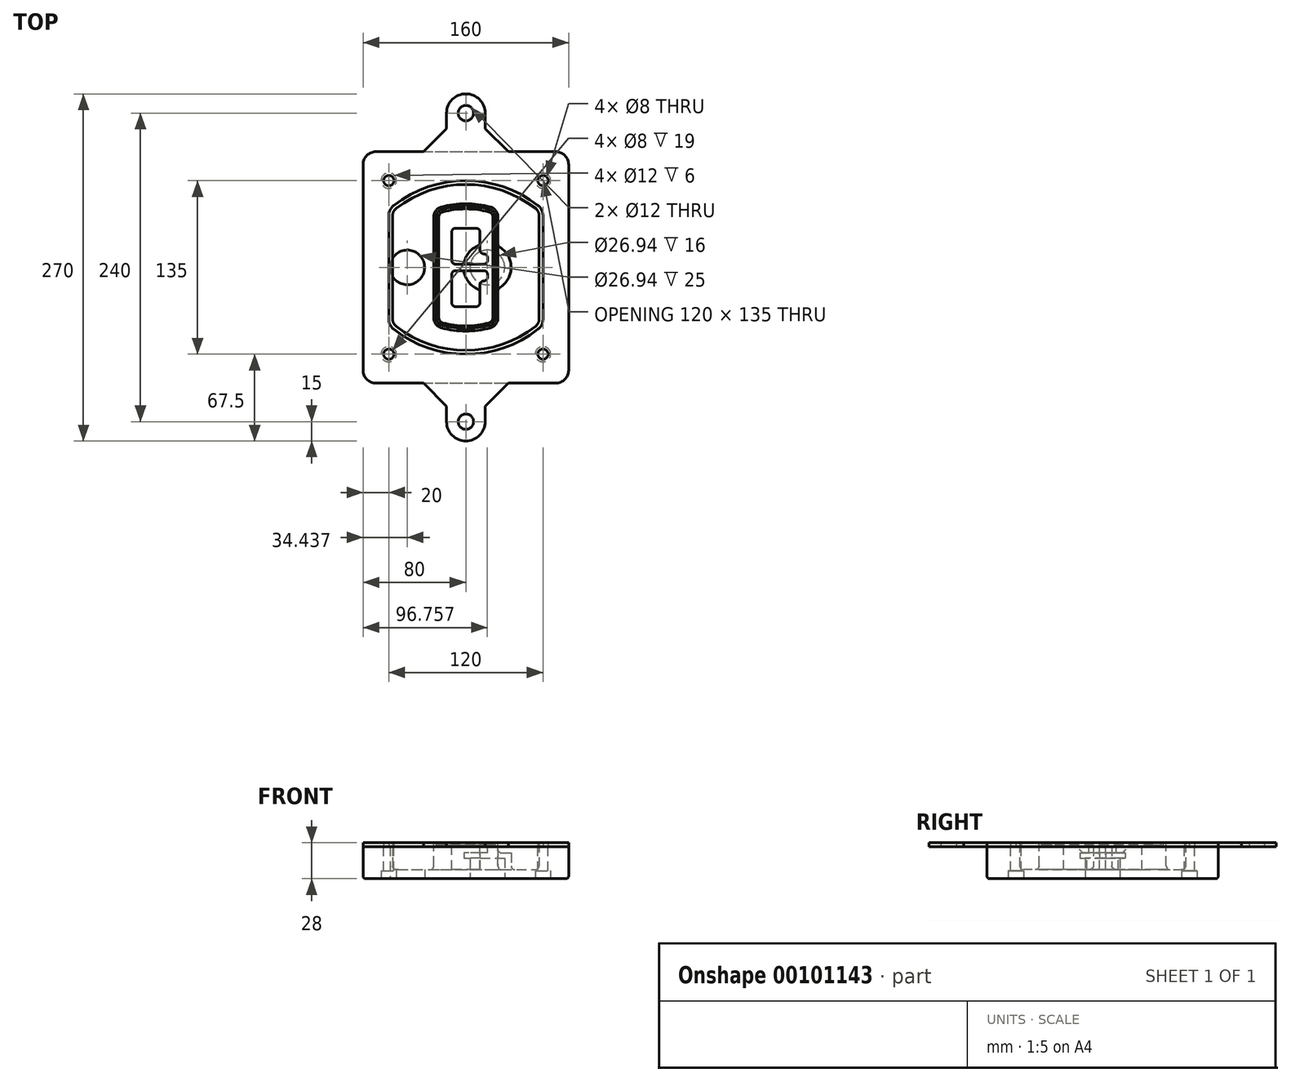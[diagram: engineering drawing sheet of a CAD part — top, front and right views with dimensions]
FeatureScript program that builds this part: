
annotation { "Feature Type Name" : "Feature", "Feature Type Description" : "" }
export const myFeature = defineFeature(function(context is Context, id is Id, definition is map)
    precondition{}
    {
        {
            var Q0;
            Q0=qCreatedBy(makeId("Top.planeOp"),FACE);
            var sketch = newSketch(context, id + "F0", { "sketchPlane" : qUnion([Q0])});
            skPoint(sketch, "E0.rect.middle", {"position": v(0, 0) * mm});
            skLineSegment(sketch, "E1.bottom", {"start": v(-70, -90) * mm, "end": v(70, -90) * mm});
            skLineSegment(sketch, "E1.top", {"start": v(-70, 90) * mm, "end": v(70, 90) * mm});
            skLineSegment(sketch, "E1.left", {"start": v(-80, -80) * mm, "end": v(-80, 80) * mm});
            skLineSegment(sketch, "E1.right", {"start": v(80, -80) * mm, "end": v(80, 80) * mm});
            skLineSegment(sketch, "E2", {"start": v(-80, 90) * mm, "end": v(80, -90) * mm, "construction": true});
            skLineSegment(sketch, "E3", {"start": v(80, 90) * mm, "end": v(-80, -90) * mm, "construction": true});
            skCircle(sketch, "E4", {"center": v(-60, 67.5) * mm, "radius": 4 * mm});
            skCircle(sketch, "E5", {"center": v(60, 67.5) * mm, "radius": 4 * mm});
            skCircle(sketch, "E6", {"center": v(60, -67.5) * mm, "radius": 4 * mm});
            skCircle(sketch, "E7", {"center": v(-60, -67.5) * mm, "radius": 4 * mm});
            skLineSegment(sketch, "E8", {"start": v(-60, 67.5) * mm, "end": v(60, 67.5) * mm, "construction": true});
            skLineSegment(sketch, "E9", {"start": v(60, 67.5) * mm, "end": v(60, -67.5) * mm, "construction": true});
            skLineSegment(sketch, "E10", {"start": v(60, -67.5) * mm, "end": v(-60, -67.5) * mm, "construction": true});
            skLineSegment(sketch, "E11", {"start": v(-60, -67.5) * mm, "end": v(-60, 67.5) * mm, "construction": true});
            skLineSegment(sketch, "E12", {"start": v(-60, 40.3) * mm, "end": v(-60, -40.3) * mm});
            skLineSegment(sketch, "E13", {"start": v(60, 40.3) * mm, "end": v(60, -40.3) * mm});
            skArc(sketch, "E14", {"start": v(56.15, 48.18) * mm, "mid": v(0, 67.5) * mm, "end": v(-56.15, 48.18) * mm});
            skArc(sketch, "E15", {"start": v(-56.15, -48.18) * mm, "mid": v(0, -67.5) * mm, "end": v(56.15, -48.18) * mm});
            skLineSegment(sketch, "E16", {"start": v(-60, 0) * mm, "end": v(60, 0) * mm, "construction": true});
            skPoint(sketch, "E17.visualSharp", {"position": v(-60, -45) * mm});
            skArc(sketch, "E17.filletArc", {"start": v(-60, -40.3) * mm, "mid": v(-58.99, -44.68) * mm, "end": v(-56.15, -48.18) * mm});
            skPoint(sketch, "E18.visualSharp", {"position": v(-60, 45) * mm});
            skArc(sketch, "E18.filletArc", {"start": v(-56.15, 48.18) * mm, "mid": v(-58.99, 44.68) * mm, "end": v(-60, 40.3) * mm});
            skPoint(sketch, "E19.visualSharp", {"position": v(60, 45) * mm});
            skArc(sketch, "E19.filletArc", {"start": v(60, 40.3) * mm, "mid": v(58.99, 44.68) * mm, "end": v(56.15, 48.18) * mm});
            skPoint(sketch, "E20.visualSharp", {"position": v(60, -45) * mm});
            skArc(sketch, "E20.filletArc", {"start": v(56.15, -48.18) * mm, "mid": v(58.99, -44.68) * mm, "end": v(60, -40.3) * mm});
            skPoint(sketch, "E21.visualSharp", {"position": v(-80, 90) * mm});
            skArc(sketch, "E21.filletArc", {"start": v(-70, 90) * mm, "mid": v(-77.07, 87.07) * mm, "end": v(-80, 80) * mm});
            skPoint(sketch, "E22.visualSharp", {"position": v(80, 90) * mm});
            skArc(sketch, "E22.filletArc", {"start": v(80, 80) * mm, "mid": v(77.07, 87.07) * mm, "end": v(70, 90) * mm});
            skPoint(sketch, "E23.visualSharp", {"position": v(80, -90) * mm});
            skArc(sketch, "E23.filletArc", {"start": v(70, -90) * mm, "mid": v(77.07, -87.07) * mm, "end": v(80, -80) * mm});
            skPoint(sketch, "E24.visualSharp", {"position": v(-80, -90) * mm});
            skArc(sketch, "E24.filletArc", {"start": v(-80, -80) * mm, "mid": v(-77.07, -87.07) * mm, "end": v(-70, -90) * mm});
            skArc(sketch, "E25.0", {"start": v(57, 40.3) * mm, "mid": v(56.3, 43.36) * mm, "end": v(54.3, 45.81) * mm});
            skLineSegment(sketch, "E25.1", {"start": v(57, 40.3) * mm, "end": v(57, -40.3) * mm});
            skArc(sketch, "E25.2", {"start": v(54.3, -45.81) * mm, "mid": v(56.3, -43.36) * mm, "end": v(57, -40.3) * mm});
            skArc(sketch, "E25.3", {"start": v(-54.3, -45.81) * mm, "mid": v(0, -64.5) * mm, "end": v(54.3, -45.81) * mm});
            skArc(sketch, "E25.4", {"start": v(-57, -40.3) * mm, "mid": v(-56.3, -43.36) * mm, "end": v(-54.3, -45.81) * mm});
            skArc(sketch, "E25.5", {"start": v(54.3, 45.81) * mm, "mid": v(0, 64.5) * mm, "end": v(-54.3, 45.81) * mm});
            skLineSegment(sketch, "E25.6", {"start": v(-57, 40.3) * mm, "end": v(-57, -40.3) * mm});
            skArc(sketch, "E25.7", {"start": v(-54.3, 45.81) * mm, "mid": v(-56.3, 43.36) * mm, "end": v(-57, 40.3) * mm});
            skArc(sketch, "E26.0", {"start": v(-58.62, 51.33) * mm, "mid": v(-62.58, 46.43) * mm, "end": v(-64, 40.3) * mm});
            skArc(sketch, "E26.1", {"start": v(58.62, 51.33) * mm, "mid": v(0, 71.5) * mm, "end": v(-58.62, 51.33) * mm});
            skArc(sketch, "E26.2", {"start": v(64, 40.3) * mm, "mid": v(62.58, 46.43) * mm, "end": v(58.62, 51.33) * mm});
            skLineSegment(sketch, "E26.3", {"start": v(64, 40.3) * mm, "end": v(64, -40.3) * mm});
            skArc(sketch, "E26.4", {"start": v(58.62, -51.33) * mm, "mid": v(62.58, -46.43) * mm, "end": v(64, -40.3) * mm});
            skLineSegment(sketch, "E26.5", {"start": v(-64, 40.3) * mm, "end": v(-64, -40.3) * mm});
            skArc(sketch, "E26.6", {"start": v(-58.62, -51.33) * mm, "mid": v(0, -71.5) * mm, "end": v(58.62, -51.33) * mm});
            skArc(sketch, "E26.7", {"start": v(-64, -40.3) * mm, "mid": v(-62.58, -46.43) * mm, "end": v(-58.62, -51.33) * mm});
            skSolve(sketch);
        }
        {
            var Q0;
            Q0=makeQuery(id+"F0.imprint","IMPRINT",FACE,{"disambiguationData":[TD([[makeQuery(id+"F0.imprint","IMPRINT",EDGE,{"derivedFrom":sQuery(id+"F0.wireOp",EDGE,"E1.bottom")}),1.0]])]});
            var Q1;
            Q1=makeQuery(id+"F0.imprint","IMPRINT",FACE,{"disambiguationData":[TD([[makeQuery(id+"F0.imprint","IMPRINT",EDGE,{"derivedFrom":sQuery(id+"F0.wireOp",EDGE,"E12")}),1.0]])]});
            var Q2;
            Q2=makeQuery(id+"F0.imprint","IMPRINT",FACE,{"disambiguationData":[TD([[makeQuery(id+"F0.imprint","IMPRINT",EDGE,{"derivedFrom":sQuery(id+"F0.wireOp",EDGE,"E25.0")}),1.0]])]});
            var Q3;
            Q3=makeQuery(id+"F0.imprint","IMPRINT",FACE,{"disambiguationData":[TD([[makeQuery(id+"F0.imprint","IMPRINT",EDGE,{"derivedFrom":sQuery(id+"F0.wireOp",EDGE,"E12")}),-1.0]])]});
            extrude(context, id + "F1", {"entities" : qUnion([Q0, Q1, Q2, Q3]), "oppositeDirection" : true, "depth" : 25 * mm});
        }
        {
            var Q0;
            Q0=makeQuery(id+"F0.imprint","IMPRINT",FACE,{"disambiguationData":[TD([[makeQuery(id+"F0.imprint","IMPRINT",EDGE,{"derivedFrom":sQuery(id+"F0.wireOp",EDGE,"E12")}),1.0]])]});
            extrude(context, id + "F2", {"entities" : qUnion([Q0]), "operationType" : NewBodyOperationType.ADD, "depth" : 3 * mm});
        }
        {
            var Q0;
            Q0=makeQuery(id+"F0.imprint","IMPRINT",FACE,{"disambiguationData":[TD([[makeQuery(id+"F0.imprint","IMPRINT",EDGE,{"derivedFrom":sQuery(id+"F0.wireOp",EDGE,"E25.0")}),1.0]])]});
            extrude(context, id + "F3", {"entities" : qUnion([Q0]), "operationType" : NewBodyOperationType.REMOVE, "oppositeDirection" : true, "depth" : 18 * mm});
        }
        {
            var Q0;
            Q0=makeQuery(id+"F2.opExtrude","CAP_FACE",FACE,{"disambiguationData":[OSD([sQuery(id+"F0.wireOp",EDGE,"E12"),sQuery(id+"F0.wireOp",EDGE,"E13"),sQuery(id+"F0.wireOp",EDGE,"E14"),sQuery(id+"F0.wireOp",EDGE,"E15"),sQuery(id+"F0.wireOp",EDGE,"E17.filletArc"),sQuery(id+"F0.wireOp",EDGE,"E18.filletArc"),sQuery(id+"F0.wireOp",EDGE,"E19.filletArc"),sQuery(id+"F0.wireOp",EDGE,"E20.filletArc"),sQuery(id+"F0.wireOp",EDGE,"E25.0"),sQuery(id+"F0.wireOp",EDGE,"E25.1"),sQuery(id+"F0.wireOp",EDGE,"E25.2"),sQuery(id+"F0.wireOp",EDGE,"E25.3"),sQuery(id+"F0.wireOp",EDGE,"E25.4"),sQuery(id+"F0.wireOp",EDGE,"E25.5"),sQuery(id+"F0.wireOp",EDGE,"E25.6"),sQuery(id+"F0.wireOp",EDGE,"E25.7")])],"isStart":false});
            var sketch = newSketch(context, id + "F4", { "sketchPlane" : qUnion([Q0])});
            skArc(sketch, "E27.0", {"start": v(-19.08, -46.97) * mm, "mid": v(0, -49.5) * mm, "end": v(19.08, -46.97) * mm});
            skArc(sketch, "E28.0", {"start": v(19.08, 46.97) * mm, "mid": v(0, 49.5) * mm, "end": v(-19.08, 46.97) * mm});
            skLineSegment(sketch, "E29", {"start": v(-25, 39.25) * mm, "end": v(-25, -39.25) * mm});
            skLineSegment(sketch, "E30", {"start": v(25, 39.25) * mm, "end": v(25, -39.25) * mm});
            skLineSegment(sketch, "E31", {"start": v(-25, 45.1) * mm, "end": v(25, 45.1) * mm, "construction": true});
            skLineSegment(sketch, "E32", {"start": v(-25, -45.1) * mm, "end": v(25, -45.1) * mm, "construction": true});
            skPoint(sketch, "E33.visualSharp", {"position": v(-25, 45.1) * mm});
            skArc(sketch, "E33.filletArc", {"start": v(-19.08, 46.97) * mm, "mid": v(-23.35, 44.11) * mm, "end": v(-25, 39.25) * mm});
            skPoint(sketch, "E34.visualSharp", {"position": v(25, 45.1) * mm});
            skArc(sketch, "E34.filletArc", {"start": v(25, 39.25) * mm, "mid": v(23.35, 44.11) * mm, "end": v(19.08, 46.97) * mm});
            skPoint(sketch, "E35.visualSharp", {"position": v(25, -45.1) * mm});
            skArc(sketch, "E35.filletArc", {"start": v(19.08, -46.97) * mm, "mid": v(23.35, -44.11) * mm, "end": v(25, -39.25) * mm});
            skPoint(sketch, "E36.visualSharp", {"position": v(-25, -45.1) * mm});
            skArc(sketch, "E36.filletArc", {"start": v(-25, -39.25) * mm, "mid": v(-23.35, -44.11) * mm, "end": v(-19.08, -46.97) * mm});
            skArc(sketch, "E37.0", {"start": v(54.3, 45.81) * mm, "mid": v(0, 64.5) * mm, "end": v(-54.3, 45.81) * mm});
            skArc(sketch, "E37.1", {"start": v(-54.3, 45.81) * mm, "mid": v(-56.3, 43.36) * mm, "end": v(-57, 40.3) * mm});
            skLineSegment(sketch, "E37.2", {"start": v(-57, 40.3) * mm, "end": v(-57, -40.3) * mm});
            skArc(sketch, "E37.3", {"start": v(-57, -40.3) * mm, "mid": v(-56.3, -43.36) * mm, "end": v(-54.3, -45.81) * mm});
            skArc(sketch, "E37.4", {"start": v(-54.3, -45.81) * mm, "mid": v(0, -64.5) * mm, "end": v(54.3, -45.81) * mm});
            skArc(sketch, "E37.5", {"start": v(54.3, -45.81) * mm, "mid": v(56.3, -43.36) * mm, "end": v(57, -40.3) * mm});
            skLineSegment(sketch, "E37.6", {"start": v(57, 40.3) * mm, "end": v(57, -40.3) * mm});
            skArc(sketch, "E37.7", {"start": v(57, 40.3) * mm, "mid": v(56.3, 43.36) * mm, "end": v(54.3, 45.81) * mm});
            skLineSegment(sketch, "E38.0", {"start": v(23, 39.25) * mm, "end": v(23, -39.25) * mm});
            skArc(sketch, "E38.1", {"start": v(18.56, -45.04) * mm, "mid": v(21.76, -42.9) * mm, "end": v(23, -39.25) * mm});
            skArc(sketch, "E38.2", {"start": v(-18.56, -45.04) * mm, "mid": v(0, -47.5) * mm, "end": v(18.56, -45.04) * mm});
            skArc(sketch, "E38.3", {"start": v(-23, -39.25) * mm, "mid": v(-21.76, -42.9) * mm, "end": v(-18.56, -45.04) * mm});
            skLineSegment(sketch, "E38.4", {"start": v(-23, 39.25) * mm, "end": v(-23, -39.25) * mm});
            skArc(sketch, "E38.5", {"start": v(23, 39.25) * mm, "mid": v(21.76, 42.9) * mm, "end": v(18.56, 45.04) * mm});
            skArc(sketch, "E38.6", {"start": v(-18.56, 45.04) * mm, "mid": v(-21.76, 42.9) * mm, "end": v(-23, 39.25) * mm});
            skArc(sketch, "E38.7", {"start": v(18.56, 45.04) * mm, "mid": v(0, 47.5) * mm, "end": v(-18.56, 45.04) * mm});
            skArc(sketch, "E39.0", {"start": v(21, 39.25) * mm, "mid": v(20.18, 41.68) * mm, "end": v(18.04, 43.1) * mm});
            skLineSegment(sketch, "E39.1", {"start": v(21, 39.25) * mm, "end": v(21, -39.25) * mm});
            skArc(sketch, "E39.2", {"start": v(18.04, -43.1) * mm, "mid": v(20.18, -41.68) * mm, "end": v(21, -39.25) * mm});
            skArc(sketch, "E39.3", {"start": v(-18.04, -43.1) * mm, "mid": v(0, -45.5) * mm, "end": v(18.04, -43.1) * mm});
            skArc(sketch, "E39.4", {"start": v(-21, -39.25) * mm, "mid": v(-20.18, -41.68) * mm, "end": v(-18.04, -43.1) * mm});
            skArc(sketch, "E39.5", {"start": v(18.04, 43.1) * mm, "mid": v(0, 45.5) * mm, "end": v(-18.04, 43.1) * mm});
            skLineSegment(sketch, "E39.6", {"start": v(-21, 39.25) * mm, "end": v(-21, -39.25) * mm});
            skArc(sketch, "E39.7", {"start": v(-18.04, 43.1) * mm, "mid": v(-20.18, 41.68) * mm, "end": v(-21, 39.25) * mm});
            skLineSegment(sketch, "E40", {"start": v(-25, 0) * mm, "end": v(25, 0) * mm, "construction": true});
            skLineSegment(sketch, "E41", {"start": v(-11, 5.5) * mm, "end": v(-11, 27.5) * mm});
            skLineSegment(sketch, "E42", {"start": v(-8, 30.5) * mm, "end": v(8, 30.5) * mm});
            skLineSegment(sketch, "E43", {"start": v(11, 27.5) * mm, "end": v(11, 13.5) * mm});
            skLineSegment(sketch, "E44", {"start": v(14, 10.5) * mm, "end": v(14, 10.5) * mm});
            skLineSegment(sketch, "E45", {"start": v(17, 7.5) * mm, "end": v(17, 5.5) * mm});
            skLineSegment(sketch, "E46", {"start": v(14, 2.5) * mm, "end": v(-8, 2.5) * mm});
            skPoint(sketch, "E47.visualSharp", {"position": v(-11, 30.5) * mm});
            skArc(sketch, "E47.filletArc", {"start": v(-8, 30.5) * mm, "mid": v(-10.12, 29.62) * mm, "end": v(-11, 27.5) * mm});
            skPoint(sketch, "E48.visualSharp", {"position": v(11, 30.5) * mm});
            skArc(sketch, "E48.filletArc", {"start": v(11, 27.5) * mm, "mid": v(10.12, 29.62) * mm, "end": v(8, 30.5) * mm});
            skPoint(sketch, "E49.visualSharp", {"position": v(11, 10.5) * mm});
            skArc(sketch, "E49.filletArc", {"start": v(11, 13.5) * mm, "mid": v(11.88, 11.38) * mm, "end": v(14, 10.5) * mm});
            skPoint(sketch, "E50.visualSharp", {"position": v(17, 10.5) * mm});
            skArc(sketch, "E50.filletArc", {"start": v(17, 7.5) * mm, "mid": v(16.12, 9.62) * mm, "end": v(14, 10.5) * mm});
            skPoint(sketch, "E51.visualSharp", {"position": v(17, 2.5) * mm});
            skArc(sketch, "E51.filletArc", {"start": v(14, 2.5) * mm, "mid": v(16.12, 3.38) * mm, "end": v(17, 5.5) * mm});
            skPoint(sketch, "E52.visualSharp", {"position": v(-11, 2.5) * mm});
            skArc(sketch, "E52.filletArc", {"start": v(-11, 5.5) * mm, "mid": v(-10.12, 3.38) * mm, "end": v(-8, 2.5) * mm});
            skLineSegment(sketch, "E53.0.MirrorCS", {"start": v(14, -2.5) * mm, "end": v(-8, -2.5) * mm});
            skArc(sketch, "E54.0.MirrorCS", {"start": v(-11, -5.5) * mm, "mid": v(-10.12, -3.38) * mm, "end": v(-8, -2.5) * mm});
            skLineSegment(sketch, "E55.0.MirrorCS", {"start": v(-11, -5.5) * mm, "end": v(-11, -27.5) * mm});
            skArc(sketch, "E56.0.MirrorCS", {"start": v(-8, -30.5) * mm, "mid": v(-10.12, -29.62) * mm, "end": v(-11, -27.5) * mm});
            skLineSegment(sketch, "E57.0.MirrorCS", {"start": v(-8, -30.5) * mm, "end": v(8, -30.5) * mm});
            skArc(sketch, "E58.0.MirrorCS", {"start": v(11, -27.5) * mm, "mid": v(10.12, -29.62) * mm, "end": v(8, -30.5) * mm});
            skLineSegment(sketch, "E59.0.MirrorCS", {"start": v(11, -27.5) * mm, "end": v(11, -13.5) * mm});
            skArc(sketch, "E60.0.MirrorCS", {"start": v(11, -13.5) * mm, "mid": v(11.88, -11.38) * mm, "end": v(14, -10.5) * mm});
            skArc(sketch, "E61.0.MirrorCS", {"start": v(17, -7.5) * mm, "mid": v(16.12, -9.62) * mm, "end": v(14, -10.5) * mm});
            skLineSegment(sketch, "E62.0.MirrorCS", {"start": v(17, -7.5) * mm, "end": v(17, -5.5) * mm});
            skArc(sketch, "E63.0.MirrorCS", {"start": v(14, -2.5) * mm, "mid": v(16.12, -3.38) * mm, "end": v(17, -5.5) * mm});
            skSolve(sketch);
        }
        {
            var Q0;
            Q0=makeQuery(id+"F4.imprint","IMPRINT",FACE,{"disambiguationData":[TD([[makeQuery(id+"F4.imprint","IMPRINT",EDGE,{"derivedFrom":sQuery(id+"F4.wireOp",EDGE,"E27.0")}),1.0]])]});
            var Q1;
            Q1=makeQuery(id+"F4.imprint","IMPRINT",FACE,{"disambiguationData":[TD([[makeQuery(id+"F4.imprint","IMPRINT",EDGE,{"derivedFrom":sQuery(id+"F4.wireOp",EDGE,"E38.0")}),-1.0]])]});
            var Q2;
            Q2=makeQuery(id+"F4.imprint","IMPRINT",FACE,{"disambiguationData":[TD([[makeQuery(id+"F4.imprint","IMPRINT",EDGE,{"derivedFrom":sQuery(id+"F4.wireOp",EDGE,"E39.0")}),1.0]])]});
            extrude(context, id + "F5", {"entities" : qUnion([Q0, Q1, Q2]), "operationType" : NewBodyOperationType.ADD, "endBound" : BoundingType.UP_TO_NEXT, "oppositeDirection" : true, "depth" : 25 * mm});
        }
        {
            var Q0;
            Q0=makeQuery(id+"F4.imprint","IMPRINT",FACE,{"disambiguationData":[TD([[makeQuery(id+"F4.imprint","IMPRINT",EDGE,{"derivedFrom":sQuery(id+"F4.wireOp",EDGE,"E38.0")}),-1.0]])]});
            extrude(context, id + "F6", {"entities" : qUnion([Q0]), "operationType" : NewBodyOperationType.REMOVE, "oppositeDirection" : true, "depth" : 2 * mm});
        }
        {
            var Q0;
            Q0=makeQuery(id+"F1.opExtrude","CAP_FACE",FACE,{"disambiguationData":[OSD([sQuery(id+"F0.wireOp",EDGE,"E1.bottom"),sQuery(id+"F0.wireOp",EDGE,"E1.top"),sQuery(id+"F0.wireOp",EDGE,"E1.left"),sQuery(id+"F0.wireOp",EDGE,"E1.right"),sQuery(id+"F0.wireOp",EDGE,"E4"),sQuery(id+"F0.wireOp",EDGE,"E5"),sQuery(id+"F0.wireOp",EDGE,"E6"),sQuery(id+"F0.wireOp",EDGE,"E7"),sQuery(id+"F0.wireOp",EDGE,"E21.filletArc"),sQuery(id+"F0.wireOp",EDGE,"E22.filletArc"),sQuery(id+"F0.wireOp",EDGE,"E23.filletArc"),sQuery(id+"F0.wireOp",EDGE,"E24.filletArc")])],"isStart":false});
            var sketch = newSketch(context, id + "F7", { "sketchPlane" : qUnion([Q0])});
            skCircle(sketch, "E64", {"center": v(16.76, 0) * mm, "radius": 13.47 * mm});
            skCircle(sketch, "E65", {"center": v(-45.56, 0) * mm, "radius": 13.47 * mm});
            skLineSegment(sketch, "E66", {"start": v(80, 0) * mm, "end": v(-80, 0) * mm});
            skCircle(sketch, "E67", {"center": v(16.76, 0) * mm, "radius": 18.47 * mm});
            skCircle(sketch, "E68", {"center": v(60, -67.5) * mm, "radius": 6 * mm});
            skCircle(sketch, "E69", {"center": v(-60, -67.5) * mm, "radius": 6 * mm});
            skCircle(sketch, "E70", {"center": v(-60, 67.5) * mm, "radius": 6 * mm});
            skCircle(sketch, "E71", {"center": v(60, 67.5) * mm, "radius": 6 * mm});
            skSolve(sketch);
        }
        {
            var Q0;
            {var subQ1=sQuery(id+"F7.wireOp",EDGE,"E66");var subQ4=sQuery(id+"F7.wireOp",EDGE,"E64");var subQ6=makeQuery(id+"F7.imprint","INTERSECT",VERTEX,{"disambiguationData":[OD(0.0)],"derivedFrom":[subQ4,subQ1]});Q0=makeQuery(id+"F7.imprint","IMPRINT",FACE,{"disambiguationData":[TD([[makeQuery(id+"F7.imprint","IMPRINT",EDGE,{"disambiguationData":[TD([[subQ6,-1.0]])],"derivedFrom":subQ4}),-1.0]])]});}
            var Q1;
            {var subQ0=sQuery(id+"F7.wireOp",EDGE,"E66");var subQ1=sQuery(id+"F7.wireOp",EDGE,"E64");var subQ3=makeQuery(id+"F7.imprint","INTERSECT",VERTEX,{"disambiguationData":[OD(0.0)],"derivedFrom":[subQ1,subQ0]});Q1=makeQuery(id+"F7.imprint","IMPRINT",FACE,{"disambiguationData":[TD([[makeQuery(id+"F7.imprint","IMPRINT",EDGE,{"disambiguationData":[TD([[subQ3,-1.0]])],"derivedFrom":subQ1}),1.0]])]});}
            var Q2;
            {var subQ0=sQuery(id+"F7.wireOp",EDGE,"E66");var subQ1=sQuery(id+"F7.wireOp",EDGE,"E64");var subQ3=makeQuery(id+"F7.imprint","INTERSECT",VERTEX,{"disambiguationData":[OD(0.0)],"derivedFrom":[subQ1,subQ0]});Q2=makeQuery(id+"F7.imprint","IMPRINT",FACE,{"disambiguationData":[TD([[makeQuery(id+"F7.imprint","IMPRINT",EDGE,{"disambiguationData":[TD([[subQ3,1.0]])],"derivedFrom":subQ1}),1.0]])]});}
            var Q3;
            {var subQ1=sQuery(id+"F7.wireOp",EDGE,"E66");var subQ4=sQuery(id+"F7.wireOp",EDGE,"E64");var subQ6=makeQuery(id+"F7.imprint","INTERSECT",VERTEX,{"disambiguationData":[OD(0.0)],"derivedFrom":[subQ4,subQ1]});Q3=makeQuery(id+"F7.imprint","IMPRINT",FACE,{"disambiguationData":[TD([[makeQuery(id+"F7.imprint","IMPRINT",EDGE,{"disambiguationData":[TD([[subQ6,1.0]])],"derivedFrom":subQ4}),-1.0]])]});}
            extrude(context, id + "F8", {"entities" : qUnion([Q0, Q1, Q2, Q3]), "operationType" : NewBodyOperationType.ADD, "oppositeDirection" : true, "depth" : 20 * mm});
        }
        {
            var Q0;
            {var subQ0=sQuery(id+"F7.wireOp",EDGE,"E66");var subQ1=sQuery(id+"F7.wireOp",EDGE,"E64");var subQ3=makeQuery(id+"F7.imprint","INTERSECT",VERTEX,{"disambiguationData":[OD(0.0)],"derivedFrom":[subQ1,subQ0]});Q0=makeQuery(id+"F7.imprint","IMPRINT",FACE,{"disambiguationData":[TD([[makeQuery(id+"F7.imprint","IMPRINT",EDGE,{"disambiguationData":[TD([[subQ3,-1.0]])],"derivedFrom":subQ1}),1.0]])]});}
            var Q1;
            {var subQ0=sQuery(id+"F7.wireOp",EDGE,"E66");var subQ1=sQuery(id+"F7.wireOp",EDGE,"E64");var subQ3=makeQuery(id+"F7.imprint","INTERSECT",VERTEX,{"disambiguationData":[OD(0.0)],"derivedFrom":[subQ1,subQ0]});Q1=makeQuery(id+"F7.imprint","IMPRINT",FACE,{"disambiguationData":[TD([[makeQuery(id+"F7.imprint","IMPRINT",EDGE,{"disambiguationData":[TD([[subQ3,1.0]])],"derivedFrom":subQ1}),1.0]])]});}
            extrude(context, id + "F9", {"entities" : qUnion([Q0, Q1]), "operationType" : NewBodyOperationType.REMOVE, "oppositeDirection" : true, "depth" : 16 * mm});
        }
        {
            var Q0;
            {var subQ0=sQuery(id+"F7.wireOp",EDGE,"E66");var subQ1=sQuery(id+"F7.wireOp",EDGE,"E65");var subQ3=makeQuery(id+"F7.imprint","INTERSECT",VERTEX,{"disambiguationData":[OD(0.0)],"derivedFrom":[subQ1,subQ0]});Q0=makeQuery(id+"F7.imprint","IMPRINT",FACE,{"disambiguationData":[TD([[makeQuery(id+"F7.imprint","IMPRINT",EDGE,{"disambiguationData":[TD([[subQ3,-1.0]])],"derivedFrom":subQ1}),1.0]])]});}
            var Q1;
            {var subQ0=sQuery(id+"F7.wireOp",EDGE,"E66");var subQ1=sQuery(id+"F7.wireOp",EDGE,"E65");var subQ3=makeQuery(id+"F7.imprint","INTERSECT",VERTEX,{"disambiguationData":[OD(0.0)],"derivedFrom":[subQ1,subQ0]});Q1=makeQuery(id+"F7.imprint","IMPRINT",FACE,{"disambiguationData":[TD([[makeQuery(id+"F7.imprint","IMPRINT",EDGE,{"disambiguationData":[TD([[subQ3,1.0]])],"derivedFrom":subQ1}),1.0]])]});}
            extrude(context, id + "F10", {"entities" : qUnion([Q0, Q1]), "operationType" : NewBodyOperationType.REMOVE, "oppositeDirection" : true, "depth" : 25 * mm});
        }
        {
            var Q0;
            Q0=makeQuery(id+"F7.imprint","IMPRINT",FACE,{"disambiguationData":[TD([[makeQuery(id+"F7.imprint","IMPRINT",EDGE,{"derivedFrom":sQuery(id+"F7.wireOp",EDGE,"E68")}),1.0]])]});
            var Q1;
            Q1=makeQuery(id+"F7.imprint","IMPRINT",FACE,{"disambiguationData":[TD([[makeQuery(id+"F7.imprint","IMPRINT",EDGE,{"derivedFrom":makeQuery(id+"F1.opExtrude","CAP_EDGE",EDGE,{"disambiguationData":[OSD([sQuery(id+"F0.wireOp",EDGE,"E5")])],"isStart":false})}),-1.0]])]});
            var Q2;
            Q2=makeQuery(id+"F7.imprint","IMPRINT",FACE,{"disambiguationData":[TD([[makeQuery(id+"F7.imprint","IMPRINT",EDGE,{"derivedFrom":sQuery(id+"F7.wireOp",EDGE,"E69")}),1.0]])]});
            var Q3;
            Q3=makeQuery(id+"F7.imprint","IMPRINT",FACE,{"disambiguationData":[TD([[makeQuery(id+"F7.imprint","IMPRINT",EDGE,{"derivedFrom":makeQuery(id+"F1.opExtrude","CAP_EDGE",EDGE,{"disambiguationData":[OSD([sQuery(id+"F0.wireOp",EDGE,"E4")])],"isStart":false})}),-1.0]])]});
            var Q4;
            Q4=makeQuery(id+"F7.imprint","IMPRINT",FACE,{"disambiguationData":[TD([[makeQuery(id+"F7.imprint","IMPRINT",EDGE,{"derivedFrom":sQuery(id+"F7.wireOp",EDGE,"E70")}),1.0]])]});
            var Q5;
            Q5=makeQuery(id+"F7.imprint","IMPRINT",FACE,{"disambiguationData":[TD([[makeQuery(id+"F7.imprint","IMPRINT",EDGE,{"derivedFrom":makeQuery(id+"F1.opExtrude","CAP_EDGE",EDGE,{"disambiguationData":[OSD([sQuery(id+"F0.wireOp",EDGE,"E7")])],"isStart":false})}),-1.0]])]});
            var Q6;
            Q6=makeQuery(id+"F7.imprint","IMPRINT",FACE,{"disambiguationData":[TD([[makeQuery(id+"F7.imprint","IMPRINT",EDGE,{"derivedFrom":sQuery(id+"F7.wireOp",EDGE,"E71")}),1.0]])]});
            var Q7;
            Q7=makeQuery(id+"F7.imprint","IMPRINT",FACE,{"disambiguationData":[TD([[makeQuery(id+"F7.imprint","IMPRINT",EDGE,{"derivedFrom":makeQuery(id+"F1.opExtrude","CAP_EDGE",EDGE,{"disambiguationData":[OSD([sQuery(id+"F0.wireOp",EDGE,"E6")])],"isStart":false})}),-1.0]])]});
            extrude(context, id + "F11", {"entities" : qUnion([Q0, Q1, Q2, Q3, Q4, Q5, Q6, Q7]), "operationType" : NewBodyOperationType.REMOVE, "oppositeDirection" : true, "depth" : 6 * mm});
        }
        {
            var Q0;
            Q0=makeQuery(id+"F9.boolean.opBoolean","COPY",FACE,{"derivedFrom":makeQuery(id+"F9.opExtrude","CAP_FACE",FACE,{"disambiguationData":[OSD([sQuery(id+"F7.wireOp",EDGE,"E64")])],"isStart":false})});
            var sketch = newSketch(context, id + "F12", { "sketchPlane" : qUnion([Q0])});
            skArc(sketch, "E72.0", {"start": v(11, 17.55) * mm, "mid": v(2.57, 11.82) * mm, "end": v(-1.54, 2.5) * mm});
            skArc(sketch, "E72.1", {"start": v(-1.54, -2.5) * mm, "mid": v(2.57, -11.82) * mm, "end": v(11, -17.55) * mm});
            skLineSegment(sketch, "E73", {"start": v(-1.54, -2.5) * mm, "end": v(14, -2.5) * mm});
            skLineSegment(sketch, "E74.0", {"start": v(14, 2.5) * mm, "end": v(-1.54, 2.5) * mm});
            skArc(sketch, "E74.1", {"start": v(14, 2.5) * mm, "mid": v(16.12, 3.38) * mm, "end": v(17, 5.5) * mm});
            skLineSegment(sketch, "E74.2", {"start": v(17, 7.5) * mm, "end": v(17, 5.5) * mm});
            skArc(sketch, "E74.3", {"start": v(17, 7.5) * mm, "mid": v(16.12, 9.62) * mm, "end": v(14, 10.5) * mm});
            skArc(sketch, "E74.4", {"start": v(11, 13.5) * mm, "mid": v(11.88, 11.38) * mm, "end": v(14, 10.5) * mm});
            skLineSegment(sketch, "E74.5", {"start": v(11, 17.55) * mm, "end": v(11, 13.5) * mm});
            skLineSegment(sketch, "E74.7", {"start": v(14, -2.5) * mm, "end": v(-1.54, -2.5) * mm});
            skArc(sketch, "E74.8", {"start": v(14, -2.5) * mm, "mid": v(16.12, -3.38) * mm, "end": v(17, -5.5) * mm});
            skLineSegment(sketch, "E74.9", {"start": v(17, -7.5) * mm, "end": v(17, -5.5) * mm});
            skArc(sketch, "E74.10", {"start": v(17, -7.5) * mm, "mid": v(16.12, -9.62) * mm, "end": v(14, -10.5) * mm});
            skArc(sketch, "E74.11", {"start": v(11, -13.5) * mm, "mid": v(11.88, -11.38) * mm, "end": v(14, -10.5) * mm});
            skLineSegment(sketch, "E74.12", {"start": v(11, -17.55) * mm, "end": v(11, -13.5) * mm});
            skPoint(sketch, "E75.orphan", {"position": v(11, -27.5) * mm});
            skPoint(sketch, "E76.orphan", {"position": v(-8, -2.5) * mm});
            skPoint(sketch, "E77.orphan", {"position": v(-8, 2.5) * mm});
            skPoint(sketch, "E78.orphan", {"position": v(11, 27.5) * mm});
            skSolve(sketch);
        }
        {
            var Q0;
            {var subQ7=sQuery(id+"F12.wireOp",EDGE,"E72.0");var subQ14=sQuery(id+"F12.wireOp",EDGE,"E72.1");var subQ16=sQuery(id+"F12.wireOp",EDGE,"E74.1");var subQ18=sQuery(id+"F12.wireOp",EDGE,"E74.8");Q0=qUnion([makeQuery(id+"F12.imprint","IMPRINT",FACE,{"disambiguationData":[TD([[makeQuery(id+"F12.imprint","IMPRINT",EDGE,{"derivedFrom":subQ7}),1.0]])]}),makeQuery(id+"F12.imprint","IMPRINT",FACE,{"disambiguationData":[TD([[makeQuery(id+"F12.imprint","IMPRINT",EDGE,{"derivedFrom":subQ14}),1.0]])]}),makeQuery(id+"F12.imprint","IMPRINT",FACE,{"disambiguationData":[TD([[makeQuery(id+"F12.imprint","IMPRINT",EDGE,{"derivedFrom":subQ16}),1.0]])]}),makeQuery(id+"F12.imprint","IMPRINT",FACE,{"disambiguationData":[TD([[makeQuery(id+"F12.imprint","IMPRINT",EDGE,{"derivedFrom":subQ18}),-1.0]])]})]);}
            var Q1;
            Q1=makeQuery(id+"F5.boolean.opBoolean","SPLIT",FACE,{"disambiguationData":[TD([makeQuery(id+"F5.opExtrude","SWEPT_FACE",FACE,{"disambiguationData":[OSD([sQuery(id+"F4.wireOp",EDGE,"E41")])]})])],"derivedFrom":makeQuery(id+"F3.boolean.opBoolean","COPY",FACE,{"derivedFrom":makeQuery(id+"F3.opExtrude","CAP_FACE",FACE,{"disambiguationData":[OSD([sQuery(id+"F0.wireOp",EDGE,"E25.0"),sQuery(id+"F0.wireOp",EDGE,"E25.1"),sQuery(id+"F0.wireOp",EDGE,"E25.2"),sQuery(id+"F0.wireOp",EDGE,"E25.3"),sQuery(id+"F0.wireOp",EDGE,"E25.4"),sQuery(id+"F0.wireOp",EDGE,"E25.5"),sQuery(id+"F0.wireOp",EDGE,"E25.6"),sQuery(id+"F0.wireOp",EDGE,"E25.7")])],"isStart":false})})});
            extrude(context, id + "F13", {"entities" : qUnion([Q0]), "operationType" : NewBodyOperationType.REMOVE, "endBound" : BoundingType.UP_TO_SURFACE, "endBoundEntityFace" : qUnion([Q1]), "depth" : 25 * mm});
        }
        {
            var Q0;
            Q0=makeQuery(id+"F3.boolean.opBoolean","COPY",EDGE,{"derivedFrom":makeQuery(id+"F3.opExtrude","CAP_EDGE",EDGE,{"disambiguationData":[OSD([sQuery(id+"F0.wireOp",EDGE,"E25.6")])],"isStart":false})});
            var Q1;
            Q1=makeQuery(id+"F8.boolean.opBoolean","INTERSECT",EDGE,{"derivedFrom":[makeQuery(id+"F5.opExtrude","SWEPT_FACE",FACE,{"disambiguationData":[OSD([sQuery(id+"F4.wireOp",EDGE,"E30")])]}),makeQuery(id+"F8.opExtrude","CAP_FACE",FACE,{"disambiguationData":[OSD([sQuery(id+"F7.wireOp",EDGE,"E67")])],"isStart":false})]});
            var Q2;
            Q2=makeQuery(id+"F8.boolean.opBoolean","INTERSECT",EDGE,{"disambiguationData":[OD(1.0)],"derivedFrom":[makeQuery(id+"F5.opExtrude","SWEPT_FACE",FACE,{"disambiguationData":[OSD([sQuery(id+"F4.wireOp",EDGE,"E30")])]}),makeQuery(id+"F8.opExtrude","SWEPT_FACE",FACE,{"disambiguationData":[OSD([sQuery(id+"F7.wireOp",EDGE,"E67")])]})]});
            var Q3;
            {var subQ0=sQuery(id+"F4.wireOp",EDGE,"E30");Q3=makeQuery(id+"F8.boolean.opBoolean","SPLIT",EDGE,{"disambiguationData":[TD([makeQuery(id+"F5.opExtrude","SWEPT_FACE",FACE,{"disambiguationData":[OSD([sQuery(id+"F4.wireOp",EDGE,"E35.filletArc")])]})])],"derivedFrom":makeQuery(id+"F5.opExtrude","CAP_EDGE",EDGE,{"disambiguationData":[OSD([subQ0])],"isStart":false})});}
            var Q4;
            {var subQ0=sQuery(id+"F0.wireOp",EDGE,"E25.7");var subQ1=sQuery(id+"F0.wireOp",EDGE,"E25.1");var subQ2=sQuery(id+"F0.wireOp",EDGE,"E25.6");var subQ3=sQuery(id+"F0.wireOp",EDGE,"E25.5");var subQ4=sQuery(id+"F0.wireOp",EDGE,"E25.4");var subQ5=sQuery(id+"F0.wireOp",EDGE,"E25.0");var subQ6=sQuery(id+"F0.wireOp",EDGE,"E25.2");var subQ7=sQuery(id+"F0.wireOp",EDGE,"E25.3");Q4=makeQuery(id+"F8.boolean.opBoolean","INTERSECT",EDGE,{"derivedFrom":[makeQuery(id+"F5.boolean.opBoolean","SPLIT",FACE,{"disambiguationData":[TD([makeQuery(id+"F2.opExtrude","SWEPT_FACE",FACE,{"disambiguationData":[OSD([subQ5])]})])],"derivedFrom":makeQuery(id+"F3.boolean.opBoolean","COPY",FACE,{"derivedFrom":makeQuery(id+"F3.opExtrude","CAP_FACE",FACE,{"disambiguationData":[OSD([subQ5,subQ1,subQ6,subQ7,subQ4,subQ3,subQ2,subQ0])],"isStart":false})})}),makeQuery(id+"F8.opExtrude","SWEPT_FACE",FACE,{"disambiguationData":[OSD([sQuery(id+"F7.wireOp",EDGE,"E67")])]})]});}
            var Q5;
            Q5=makeQuery(id+"F8.boolean.opBoolean","INTERSECT",EDGE,{"disambiguationData":[OD(0.0)],"derivedFrom":[makeQuery(id+"F5.opExtrude","SWEPT_FACE",FACE,{"disambiguationData":[OSD([sQuery(id+"F4.wireOp",EDGE,"E30")])]}),makeQuery(id+"F8.opExtrude","SWEPT_FACE",FACE,{"disambiguationData":[OSD([sQuery(id+"F7.wireOp",EDGE,"E67")])]})]});
            fillet(context, id + "F14", {"entities" : qUnion([Q0, Q1, Q2, Q3, Q4, Q5]), "radius" : 3 * mm, "tangentPropagation" : true, "allowEdgeOverflow" : false});
        }
        {
            var Q0;
            Q0=makeQuery(id+"F1.opExtrude","CAP_EDGE",EDGE,{"disambiguationData":[OSD([sQuery(id+"F0.wireOp",EDGE,"E1.bottom")])],"isStart":false});
            fillet(context, id + "F15", {"entities" : qUnion([Q0]), "radius" : 2 * mm, "tangentPropagation" : true, "allowEdgeOverflow" : false});
        }
        {
            var Q0;
            {var subQ0=sQuery(id+"F0.wireOp",EDGE,"E22.filletArc");var subQ1=sQuery(id+"F0.wireOp",EDGE,"E7");var subQ2=sQuery(id+"F0.wireOp",EDGE,"E6");var subQ3=sQuery(id+"F0.wireOp",EDGE,"E5");var subQ4=sQuery(id+"F0.wireOp",EDGE,"E4");var subQ5=sQuery(id+"F0.wireOp",EDGE,"E1.bottom");var subQ6=sQuery(id+"F0.wireOp",EDGE,"E21.filletArc");var subQ7=sQuery(id+"F0.wireOp",EDGE,"E1.top");var subQ8=sQuery(id+"F0.wireOp",EDGE,"E1.left");var subQ9=sQuery(id+"F0.wireOp",EDGE,"E1.right");var subQ10=sQuery(id+"F0.wireOp",EDGE,"E23.filletArc");var subQ11=sQuery(id+"F0.wireOp",EDGE,"E24.filletArc");Q0=makeQuery(id+"F2.boolean.opBoolean","SPLIT",FACE,{"disambiguationData":[TD([makeQuery(id+"F1.opExtrude","SWEPT_FACE",FACE,{"disambiguationData":[OSD([subQ5])]})])],"derivedFrom":makeQuery(id+"F1.opExtrude","CAP_FACE",FACE,{"disambiguationData":[OSD([subQ5,subQ7,subQ8,subQ9,subQ4,subQ3,subQ2,subQ1,subQ6,subQ0,subQ10,subQ11])],"isStart":true})});}
            var sketch = newSketch(context, id + "F16", { "sketchPlane" : qUnion([Q0])});
            skLineSegment(sketch, "E79", {"start": v(-33, 90) * mm, "end": v(-15, 108) * mm});
            skLineSegment(sketch, "E80", {"start": v(-15, 108) * mm, "end": v(-15, 120) * mm});
            skLineSegment(sketch, "E81", {"start": v(15, 120) * mm, "end": v(15, 108) * mm});
            skLineSegment(sketch, "E82", {"start": v(15, 108) * mm, "end": v(33, 90) * mm});
            skArc(sketch, "E83", {"start": v(15, 120) * mm, "mid": v(0, 135) * mm, "end": v(-15, 120) * mm});
            skCircle(sketch, "E84", {"center": v(0, 120) * mm, "radius": 6 * mm});
            skLineSegment(sketch, "E85", {"start": v(0, 120) * mm, "end": v(0, 90) * mm, "construction": true});
            skLineSegment(sketch, "E86", {"start": v(-80, 0) * mm, "end": v(80, 0) * mm, "construction": true});
            skLineSegment(sketch, "E87.MirrorCS", {"start": v(15, -108) * mm, "end": v(33, -90) * mm});
            skArc(sketch, "E88.MirrorCS", {"start": v(15, -120) * mm, "mid": v(0, -135) * mm, "end": v(-15, -120) * mm});
            skLineSegment(sketch, "E89.MirrorCS", {"start": v(-15, -108) * mm, "end": v(-15, -120) * mm});
            skLineSegment(sketch, "E90.MirrorCS", {"start": v(-33, -90) * mm, "end": v(-15, -108) * mm});
            skLineSegment(sketch, "E91.MirrorCS", {"start": v(15, -120) * mm, "end": v(15, -108) * mm});
            skCircle(sketch, "E92.MirrorC", {"center": v(0, -120) * mm, "radius": 6 * mm});
            skLineSegment(sketch, "E93.MirrorCS", {"start": v(0, -120) * mm, "end": v(0, -90) * mm, "construction": true});
            skSolve(sketch);
        }
        {
            var Q0;
            Q0=makeQuery(id+"F16.imprint","IMPRINT",FACE,{"disambiguationData":[TD([[makeQuery(id+"F16.imprint","IMPRINT",EDGE,{"derivedFrom":makeQuery(id+"F1.opExtrude","CAP_EDGE",EDGE,{"disambiguationData":[OSD([sQuery(id+"F0.wireOp",EDGE,"E1.left")])],"isStart":true})}),-1.0]])]});
            var Q1;
            {var subQ1=sQuery(id+"F16.wireOp",EDGE,"E87.MirrorCS");Q1=makeQuery(id+"F16.imprint","IMPRINT",FACE,{"disambiguationData":[TD([[makeQuery(id+"F16.imprint","IMPRINT",EDGE,{"derivedFrom":subQ1}),1.0]])]});}
            var Q2;
            {var subQ1=sQuery(id+"F16.wireOp",EDGE,"E79");Q2=makeQuery(id+"F16.imprint","IMPRINT",FACE,{"disambiguationData":[TD([[makeQuery(id+"F16.imprint","IMPRINT",EDGE,{"derivedFrom":subQ1}),-1.0]])]});}
            var Q3;
            Q3=makeQuery(id+"F2.opExtrude","CAP_FACE",FACE,{"disambiguationData":[OSD([sQuery(id+"F0.wireOp",EDGE,"E12"),sQuery(id+"F0.wireOp",EDGE,"E13"),sQuery(id+"F0.wireOp",EDGE,"E14"),sQuery(id+"F0.wireOp",EDGE,"E15"),sQuery(id+"F0.wireOp",EDGE,"E17.filletArc"),sQuery(id+"F0.wireOp",EDGE,"E18.filletArc"),sQuery(id+"F0.wireOp",EDGE,"E19.filletArc"),sQuery(id+"F0.wireOp",EDGE,"E20.filletArc"),sQuery(id+"F0.wireOp",EDGE,"E25.0"),sQuery(id+"F0.wireOp",EDGE,"E25.1"),sQuery(id+"F0.wireOp",EDGE,"E25.2"),sQuery(id+"F0.wireOp",EDGE,"E25.3"),sQuery(id+"F0.wireOp",EDGE,"E25.4"),sQuery(id+"F0.wireOp",EDGE,"E25.5"),sQuery(id+"F0.wireOp",EDGE,"E25.6"),sQuery(id+"F0.wireOp",EDGE,"E25.7")])],"isStart":false});
            extrude(context, id + "F17", {"entities" : qUnion([Q0, Q1, Q2]), "endBound" : BoundingType.UP_TO_SURFACE, "endBoundEntityFace" : qUnion([Q3]), "depth" : 25 * mm});
        }
    });
